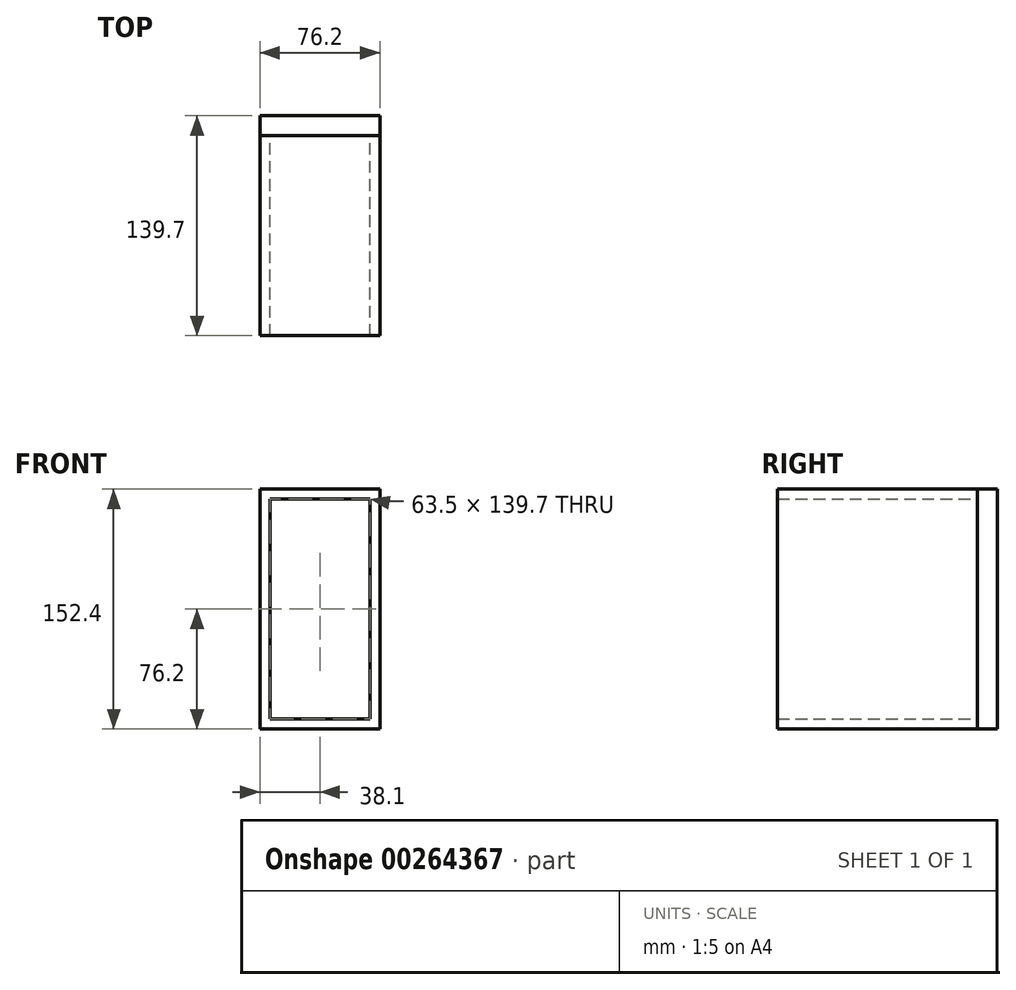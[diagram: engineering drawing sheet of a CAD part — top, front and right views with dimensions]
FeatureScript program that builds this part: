
annotation { "Feature Type Name" : "Feature", "Feature Type Description" : "" }
export const myFeature = defineFeature(function(context is Context, id is Id, definition is map)
    precondition{}
    {
        {
            var Q0;
            Q0=qCreatedBy(makeId("Front.planeOp"),FACE);
            var sketch = newSketch(context, id + "F0", { "sketchPlane" : qUnion([Q0])});
            skLineSegment(sketch, "E0.bottom", {"start": v(38.1, 76.2) * mm, "end": v(-38.1, 76.2) * mm});
            skLineSegment(sketch, "E0.top", {"start": v(38.1, -76.2) * mm, "end": v(-38.1, -76.2) * mm});
            skLineSegment(sketch, "E0.left", {"start": v(38.1, 76.2) * mm, "end": v(38.1, -76.2) * mm});
            skLineSegment(sketch, "E0.right", {"start": v(-38.1, 76.2) * mm, "end": v(-38.1, -76.2) * mm});
            skPoint(sketch, "E0.middle", {"position": v(0, 0) * mm});
            skLineSegment(sketch, "E1.bottom", {"start": v(31.75, 69.85) * mm, "end": v(-31.75, 69.85) * mm});
            skLineSegment(sketch, "E1.top", {"start": v(31.75, -69.85) * mm, "end": v(-31.75, -69.85) * mm});
            skLineSegment(sketch, "E1.left", {"start": v(31.75, 69.85) * mm, "end": v(31.75, -69.85) * mm});
            skLineSegment(sketch, "E1.right", {"start": v(-31.75, 69.85) * mm, "end": v(-31.75, -69.85) * mm});
            skSolve(sketch);
        }
        {
            var Q0;
            Q0 = qSketchRegion(id + "F0", true);
            extrude(context, id + "F1", {"entities" : qUnion([Q0]), "depth" : 127 * mm});
        }
        {
            var Q0;
            Q0=makeQuery(id+"F0.imprint","IMPRINT",FACE,{"disambiguationData":[TD([[makeQuery(id+"F0.imprint","IMPRINT",EDGE,{"derivedFrom":sQuery(id+"F0.wireOp",EDGE,"E0.bottom")}),1.0]])]});
            var Q1;
            Q1=makeQuery(id+"F0.imprint","IMPRINT",FACE,{"disambiguationData":[TD([[makeQuery(id+"F0.imprint","IMPRINT",EDGE,{"derivedFrom":sQuery(id+"F0.wireOp",EDGE,"E1.bottom")}),1.0]])]});
            extrude(context, id + "F2", {"entities" : qUnion([Q0, Q1]), "oppositeDirection" : true, "depth" : 12.7 * mm});
        }
    });
